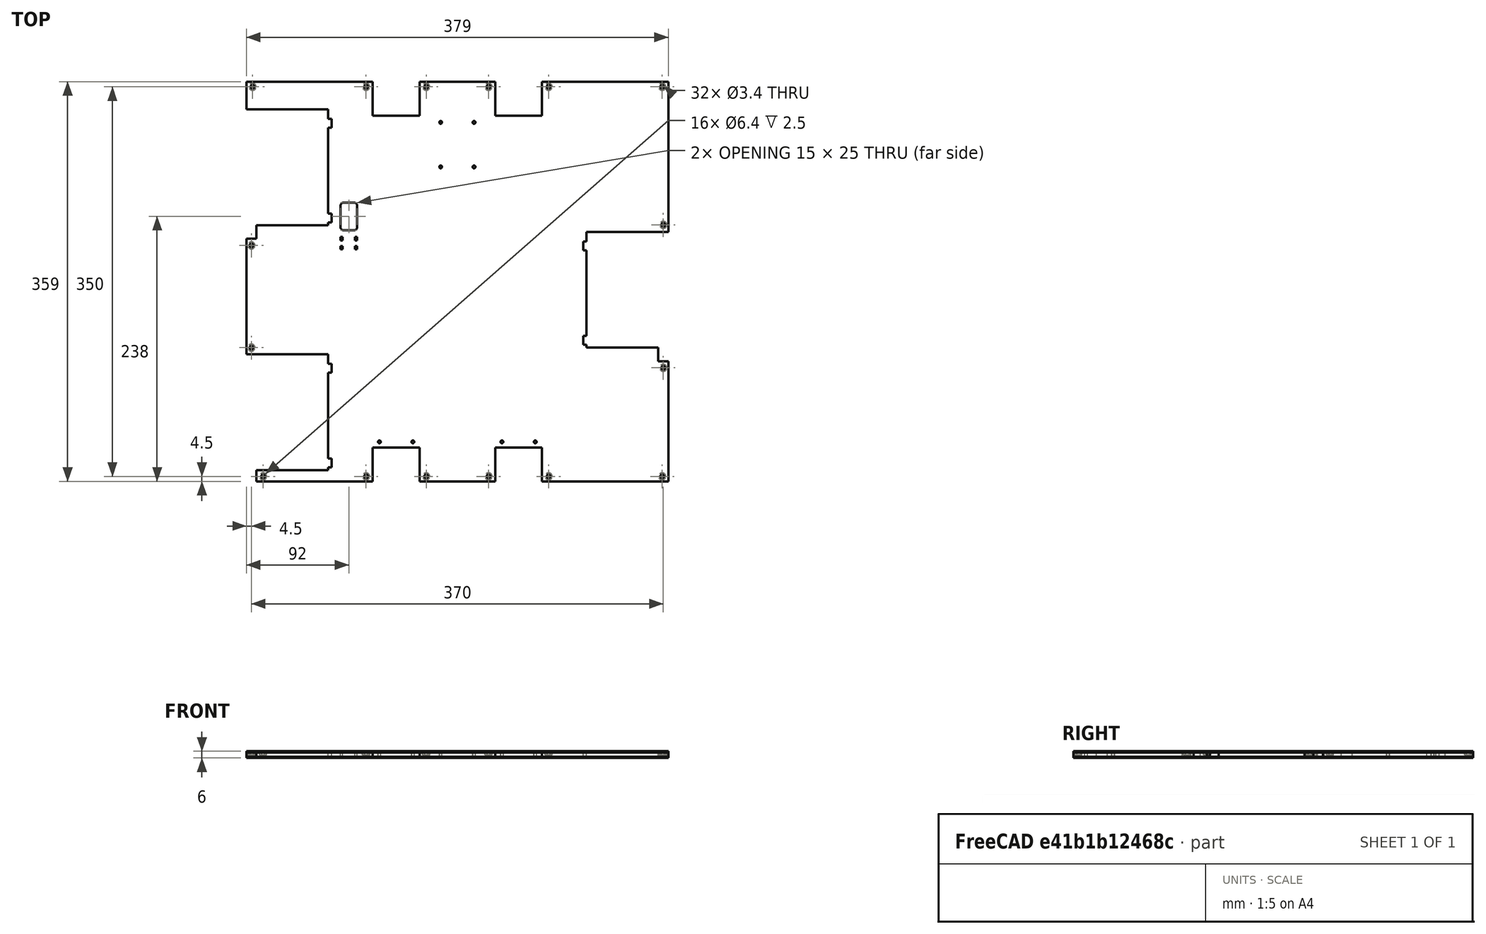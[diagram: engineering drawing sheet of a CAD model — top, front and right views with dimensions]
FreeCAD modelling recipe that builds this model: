
FCSTD DOCUMENT  (FreeCAD 0.19R24291 (Git))
Label: bottom-plate-250-laser-cut
License: All rights reserved
LicenseURL: http://en.wikipedia.org/wiki/All_rights_reserved
objects: Part::Feature×20, Part::Box×10, Part::MultiFuse×10, Part::Cylinder×8, Part::Cut×6, Part::Fillet×1, Part::Extrusion×1
note: 56 computed .brp shape members not serialized (recipe doc carries the construction recipe); baked Part::Feature solids carry a one-line shape summary decoded from their .brp

FEATURE [Part::Feature] Fusion005017  label="bolt-slot_D004"
  Placement = pos=(82,-175,0) rot=(0,0,1;0rad)
  shape: bbox 6.4 x 6.4 x 6 mm, 7 faces (baked)
FEATURE [Part::Cylinder] Cylinder
  Angle = 360
  AttacherType = Attacher::AttachEngine3D
  Height = 10
  Placement = pos=(-70,-144,0) rot=(0,0,1;0rad)
  Radius = 1.25
FEATURE [Part::Cylinder] Cylinder004
  Angle = 360
  AttacherType = Attacher::AttachEngine3D
  Height = 10
  Placement = pos=(-15,143,0) rot=(0,0,1;0rad)
  Radius = 1.25
FEATURE [Part::Cylinder] Cylinder005
  Angle = 360
  AttacherType = Attacher::AttachEngine3D
  Height = 10
  Placement = pos=(15,143,0) rot=(0,0,1;0rad)
  Radius = 1.25
FEATURE [Part::Feature] Part__Mirroring002  label="motor-cut-slot002 (Mirror #1)001"
  Placement = pos=(0,110,0) rot=(0,0,1;0rad)
  shape: bbox 77 x 116.1 x 10 mm, 16 faces (baked)
FEATURE [Part::Feature] Fusion005010  label="bolt-slot_U004"
  Placement = pos=(82,175,0) rot=(0,0,1;0rad)
  shape: bbox 6.4 x 6.4 x 6 mm, 7 faces (baked)
FEATURE [Part::Feature] Cut001003002002  label="motor-cut-slot001"
  Placement = pos=(-190,40,0) rot=(0,0,1;0rad)
  shape: bbox 77 x 116.1 x 10 mm, 16 faces (baked)
FEATURE [Part::Feature] Fusion005023  label="bolt-slot_L003"
  Placement = pos=(-185,-59.36,0) rot=(0,0,1;0rad)
  shape: bbox 6.4 x 6.4 x 6 mm, 7 faces (baked)
FEATURE [Part::Box] Box  label="Cube"
  AttacherType = Attacher::AttachEngine3D
  Height = 5
  Length = 379
  Placement = pos=(-189.5,-179.5,0) rot=(0,0,1;0rad)
  Width = 359
FEATURE [Part::Cylinder] Cylinder001
  Angle = 360
  AttacherType = Attacher::AttachEngine3D
  Height = 10
  Placement = pos=(70,-144,0) rot=(0,0,1;0rad)
  Radius = 1.25
FEATURE [Part::Cylinder] Cylinder006
  Angle = 360
  AttacherType = Attacher::AttachEngine3D
  Height = 10
  Placement = pos=(15,103,0) rot=(0,0,1;0rad)
  Radius = 1.25
FEATURE [Part::Feature] Fusion005016  label="bolt-slot_D003"
  Placement = pos=(-82,-175,0) rot=(0,0,1;0rad)
  shape: bbox 6.4 x 6.4 x 6 mm, 7 faces (baked)
FEATURE [Part::Box] Box020  label="Cube012"
  AttacherType = Attacher::AttachEngine3D
  Height = 10
  Length = 2
  Placement = pos=(-105,29,0) rot=(0,0,1;0rad)
  Width = 3
FEATURE [Part::Feature] Fusion005012  label="bolt-slot_U006"
  Placement = pos=(28,175,0) rot=(0,0,1;0rad)
  shape: bbox 6.4 x 6.4 x 6 mm, 7 faces (baked)
FEATURE [Part::Box] Box007  label="end-cut002"
  AttacherType = Attacher::AttachEngine3D
  Height = 10
  Length = 42
  Placement = pos=(34,149,0) rot=(0,0,1;0rad)
  Width = 31
FEATURE [Part::Feature] Fusion005018  label="bolt-slot_D005"
  Placement = pos=(-28,-175,0) rot=(0,0,1;0rad)
  shape: bbox 6.4 x 6.4 x 6 mm, 7 faces (baked)
FEATURE [Part::Feature] Fusion005027  label="bolt-slot_R002"
  Placement = pos=(185,-77.5,0) rot=(0,0,1;0rad)
  shape: bbox 6.4 x 6.4 x 6 mm, 7 faces (baked)
FEATURE [Part::Feature] Fusion005009  label="bolt-slot_U003"
  Placement = pos=(-82,175,0) rot=(0,0,1;0rad)
  shape: bbox 6.4 x 6.4 x 6 mm, 7 faces (baked)
FEATURE [Part::Box] Box022  label="Cube014"
  AttacherType = Attacher::AttachEngine3D
  Height = 10
  Length = 2
  Placement = pos=(-92,37,0) rot=(0,0,1;0rad)
  Width = 3
FEATURE [Part::Box] Box018  label="Cube010"
  AttacherType = Attacher::AttachEngine3D
  Height = 10
  Length = 15
  Placement = pos=(-105,46,0) rot=(0,0,1;0rad)
  Width = 25
FEATURE [Part::Fillet] Fillet
  Base = -> Box018
  Edges = 4 edges r=3: [Edge1,Edge3,Edge5,Edge7]
FEATURE [Part::Feature] Fusion005011  label="bolt-slot_U005"
  Placement = pos=(-28,175,0) rot=(0,0,1;0rad)
  shape: bbox 6.4 x 6.4 x 6 mm, 7 faces (baked)
FEATURE [Part::Feature] Fusion005026  label="bolt-slot_R001"
  Placement = pos=(185,50.94,0) rot=(0,0,1;0rad)
  shape: bbox 6.4 x 6.4 x 6 mm, 7 faces (baked)
FEATURE [Part::Box] Box008  label="end-cut003"
  AttacherType = Attacher::AttachEngine3D
  Height = 10
  Length = 42
  Placement = pos=(-76,149,0) rot=(0,0,1;0rad)
  Width = 31
FEATURE [Part::Feature] Fusion005008  label="bolt-slot_U002"
  Placement = pos=(184,175,0) rot=(0,0,1;0rad)
  shape: bbox 6.4 x 6.4 x 6 mm, 7 faces (baked)
FEATURE [Part::Cylinder] Cylinder002
  Angle = 360
  AttacherType = Attacher::AttachEngine3D
  Height = 10
  Placement = pos=(-40,-144,0) rot=(0,0,1;0rad)
  Radius = 1.25
FEATURE [Part::Box] Box019  label="Cube011"
  AttacherType = Attacher::AttachEngine3D
  Height = 10
  Length = 2
  Placement = pos=(-105,37,0) rot=(0,0,1;0rad)
  Width = 3
FEATURE [Part::Feature] Fusion005015  label="bolt-slot_D002"
  Placement = pos=(184,-175,0) rot=(0,0,1;0rad)
  shape: bbox 6.4 x 6.4 x 6 mm, 7 faces (baked)
FEATURE [Part::Feature] Fusion005014  label="bolt-slot_D001"
  Placement = pos=(-174.5,-175,0) rot=(0,0,1;0rad)
  shape: bbox 6.4 x 6.4 x 6 mm, 7 faces (baked)
FEATURE [Part::Feature] Fusion005019  label="bolt-slot_D006"
  Placement = pos=(28,-175,0) rot=(0,0,1;0rad)
  shape: bbox 6.4 x 6.4 x 6 mm, 7 faces (baked)
FEATURE [Part::MultiFuse] Fusion005020
  Shapes = -> [Fusion005014,Fusion005015,Fusion005016,Fusion005017,Fusion005018,Fusion005019]
FEATURE [Part::Box] Box021  label="Cube013"
  AttacherType = Attacher::AttachEngine3D
  Height = 10
  Length = 2
  Placement = pos=(-92,29,0) rot=(0,0,1;0rad)
  Width = 3
FEATURE [Part::MultiFuse] Fusion005030
  Shapes = -> [Box019,Box020,Box021,Box022,Fillet]
FEATURE [Part::Cylinder] Cylinder003
  Angle = 360
  AttacherType = Attacher::AttachEngine3D
  Height = 10
  Placement = pos=(40,-144,0) rot=(0,0,1;0rad)
  Radius = 1.25
FEATURE [Part::MultiFuse] Fusion005028
  Shapes = -> [Fusion005027,Fusion005026]
FEATURE [Part::Feature] Cut001003002001  label="motor-cut-slot"
  Placement = pos=(-190,-180,0) rot=(0,0,1;0rad)
  shape: bbox 77 x 116.1 x 10 mm, 16 faces (baked)
FEATURE [Part::MultiFuse] Fusion
  Shapes = -> [Cut001003002001,Cut001003002002,Part__Mirroring002]
FEATURE [Part::Cut] Cut
  Base = -> Box
  Tool = -> Fusion
FEATURE [Part::Feature] Fusion005007  label="bolt-slot_U001"
  Placement = pos=(-184,175,0) rot=(0,0,1;0rad)
  shape: bbox 6.4 x 6.4 x 6 mm, 7 faces (baked)
FEATURE [Part::MultiFuse] Fusion005013
  Shapes = -> [Fusion005012,Fusion005008,Fusion005009,Fusion005010,Fusion005011,Fusion005007]
FEATURE [Part::Cylinder] Cylinder007
  Angle = 360
  AttacherType = Attacher::AttachEngine3D
  Height = 10
  Placement = pos=(-15,103,0) rot=(0,0,1;0rad)
  Radius = 1.25
FEATURE [Part::Feature] Fusion005024  label="bolt-slot_L004"
  Placement = pos=(-185,32.5,0) rot=(0,0,1;0rad)
  shape: bbox 6.4 x 6.4 x 6 mm, 7 faces (baked)
FEATURE [Part::Box] Box006  label="end-cut001"
  AttacherType = Attacher::AttachEngine3D
  Height = 10
  Length = 42
  Placement = pos=(34,-180,0) rot=(0,0,1;0rad)
  Width = 31
FEATURE [Part::Box] Box005  label="end-cut"
  AttacherType = Attacher::AttachEngine3D
  Height = 10
  Length = 42
  Placement = pos=(-76,-180,0) rot=(0,0,1;0rad)
  Width = 31
FEATURE [Part::MultiFuse] Fusion001
  Shapes = -> [Box008,Box005,Box006,Box007]
FEATURE [Part::Cut] Cut001003002003
  Base = -> Cut
  Tool = -> Fusion001
FEATURE [Part::MultiFuse] Fusion005030003
  Shapes = -> [Cylinder002,Cylinder003,Cylinder,Cylinder001]
FEATURE [Part::Cut] Cut001003002004
  Base = -> Cut001003002003
  Tool = -> Fusion005030003
FEATURE [Part::Cut] Cut001003002005
  Base = -> Cut001003002004
  Tool = -> Fusion005030
FEATURE [Part::MultiFuse] Fusion005030004
  Shapes = -> [Cylinder005,Cylinder004,Cylinder006,Cylinder007]
FEATURE [Part::MultiFuse] Fusion005030005
  Shapes = -> [Fusion005024,Fusion005023]
FEATURE [Part::Feature] Cut001003002007_cs
  shape: bbox 379 x 359 x 3e-07 mm, 0 faces, 0 solids (baked)
FEATURE [Part::MultiFuse] Fusion005030006
  Shapes = -> [Fusion005013,Fusion005020,Fusion005028,Fusion005030005]
FEATURE [Part::Cut] Cut001003002006
  Base = -> Cut001003002005
  Tool = -> Fusion005030004
FEATURE [Part::Cut] Cut001003002007
  Base = -> Cut001003002006
  Tool = -> Fusion005030006
FEATURE [Part::Extrusion] Extrude
  Base = -> Cut001003002007_cs
  Dir = (0,0,1)
  DirMode = 2
  FaceMakerClass = Part::FaceMakerBullseye
  LengthFwd = 5
  LengthRev = 0
  Solid = true
  Symmetric = false
